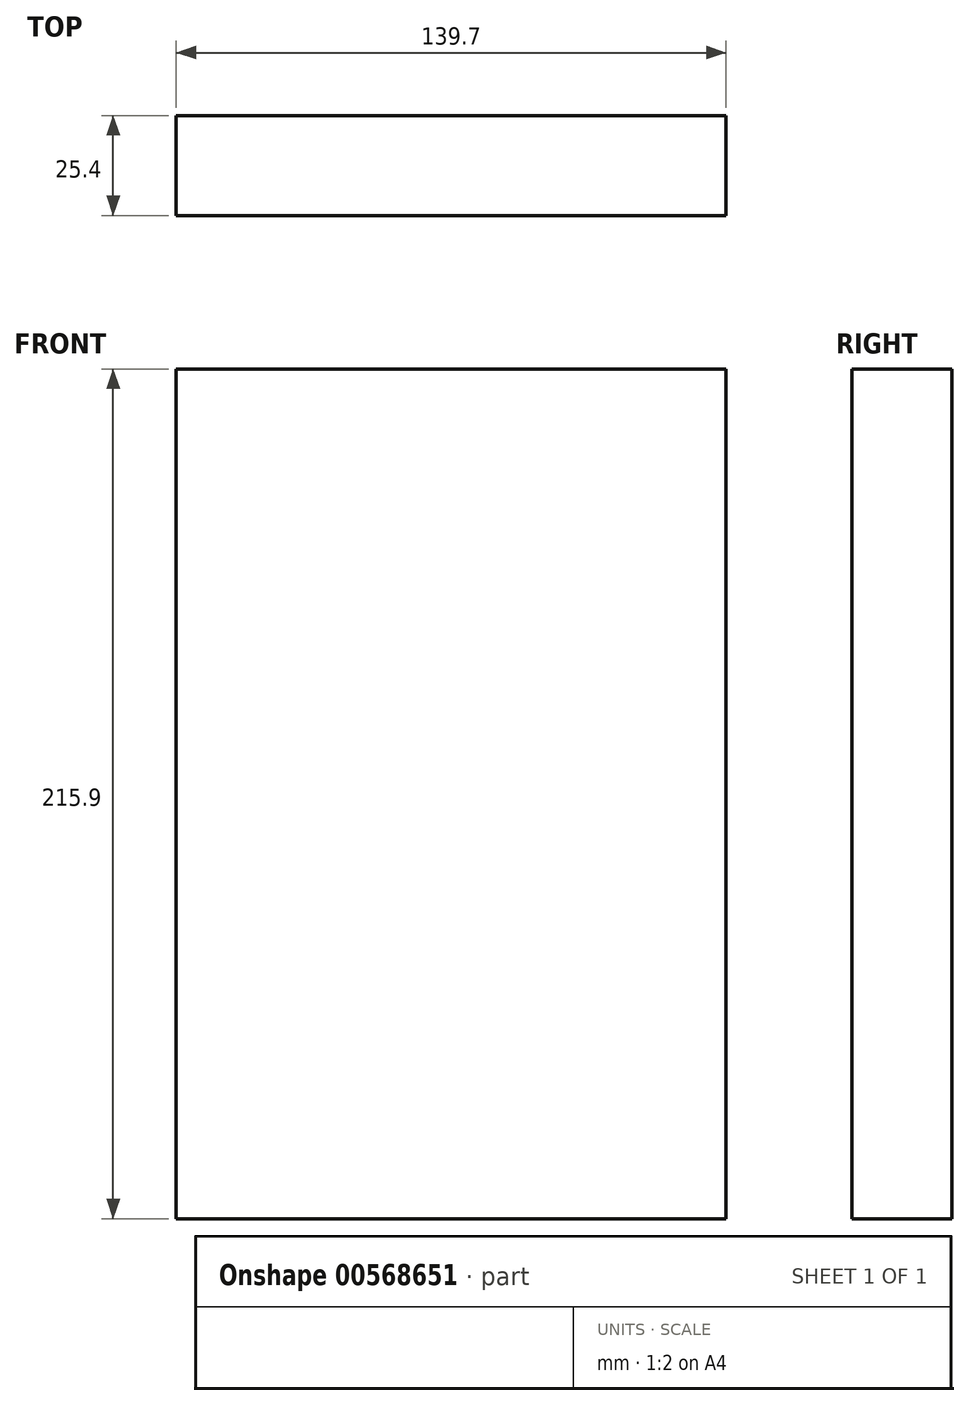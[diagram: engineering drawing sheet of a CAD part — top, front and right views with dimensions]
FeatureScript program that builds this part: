
annotation { "Feature Type Name" : "Feature", "Feature Type Description" : "" }
export const myFeature = defineFeature(function(context is Context, id is Id, definition is map)
    precondition{}
    {
        {
            var Q0;
            Q0=qCreatedBy(makeId("Front.planeOp"),FACE);
            var sketch = newSketch(context, id + "F0", { "sketchPlane" : qUnion([Q0])});
            skLineSegment(sketch, "E0", {"start": v(-76.46, 112.53) * mm, "end": v(-76.46, -103.37) * mm});
            skLineSegment(sketch, "E1", {"start": v(-76.46, -103.37) * mm, "end": v(63.24, -103.37) * mm});
            skLineSegment(sketch, "E2", {"start": v(63.24, -103.37) * mm, "end": v(63.24, 112.53) * mm});
            skLineSegment(sketch, "E3", {"start": v(63.24, 112.53) * mm, "end": v(-76.46, 112.53) * mm});
            skSolve(sketch);
        }
        {
            var Q0;
            Q0 = qSketchRegion(id + "F0", true);
            extrude(context, id + "F1", {"entities" : qUnion([Q0]), "depth" : 25.4 * mm, "offsetDistance" : 25.4 * mm});
        }
    });
